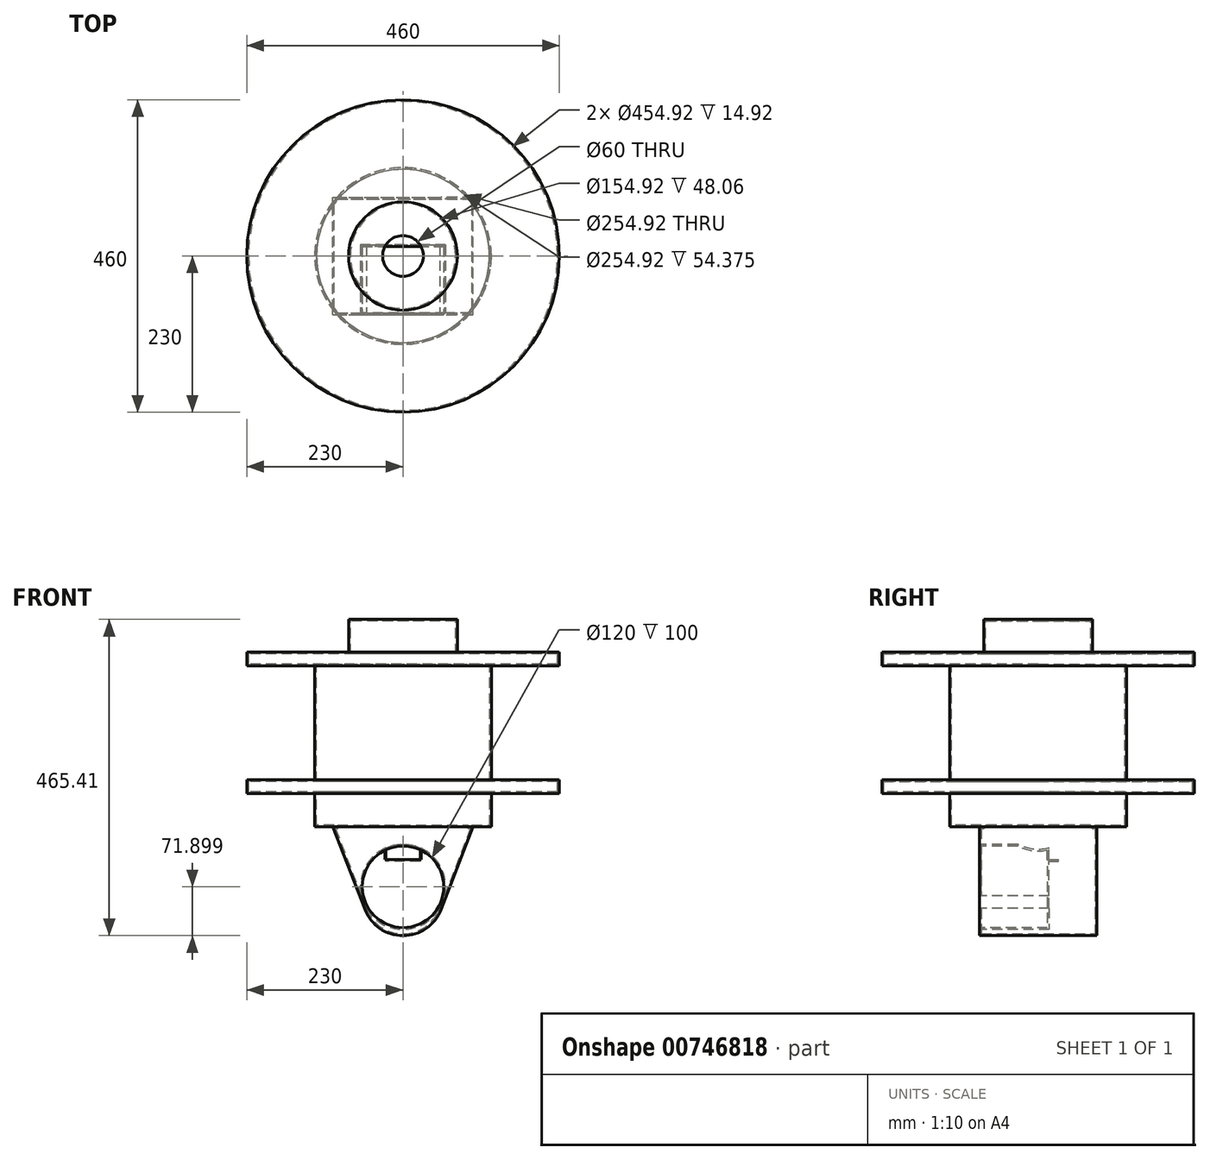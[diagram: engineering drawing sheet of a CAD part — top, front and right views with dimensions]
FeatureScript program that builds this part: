
annotation { "Feature Type Name" : "Feature", "Feature Type Description" : "" }
export const myFeature = defineFeature(function(context is Context, id is Id, definition is map)
    precondition{}
    {
        {
            var Q0;
            Q0=qCreatedBy(makeId("Front.planeOp"),FACE);
            var sketch = newSketch(context, id + "F0", { "sketchPlane" : qUnion([Q0])});
            skLineSegment(sketch, "E0", {"start": v(0, 412.84) * mm, "end": v(0, -278.5) * mm, "construction": true});
            skLineSegment(sketch, "E1", {"start": v(-30, 291.04) * mm, "end": v(-80, 291.04) * mm});
            skLineSegment(sketch, "E2", {"start": v(-80, 291.04) * mm, "end": v(-80, 242.99) * mm});
            skLineSegment(sketch, "E3", {"start": v(-80, 242.99) * mm, "end": v(-230, 242.99) * mm});
            skLineSegment(sketch, "E4", {"start": v(-230, 242.99) * mm, "end": v(-230, 222.99) * mm});
            skLineSegment(sketch, "E5", {"start": v(-230, 222.99) * mm, "end": v(-130, 222.99) * mm});
            skLineSegment(sketch, "E6", {"start": v(-130, 222.99) * mm, "end": v(-130, 54.93) * mm});
            skLineSegment(sketch, "E7", {"start": v(-130, 54.93) * mm, "end": v(-230, 54.93) * mm});
            skLineSegment(sketch, "E8", {"start": v(-230, 54.93) * mm, "end": v(-230, 34.93) * mm});
            skLineSegment(sketch, "E9", {"start": v(-230, 34.93) * mm, "end": v(-130, 34.93) * mm});
            skLineSegment(sketch, "E10", {"start": v(-130, 34.93) * mm, "end": v(-130, -14.37) * mm});
            skLineSegment(sketch, "E11", {"start": v(-130, -14.37) * mm, "end": v(-30, -14.37) * mm});
            skLineSegment(sketch, "E12", {"start": v(-30, -14.37) * mm, "end": v(-30, 291.04) * mm});
            skSolve(sketch);
        }
        {
            var Q0;
            Q0 = qSketchRegion(id + "F0", true);
            var Q1;
            Q1=sQuery(id+"F0.wireOp",EDGE,"E0");
            revolve(context, id + "F1", {"surfaceOperationType" : NewSurfaceOperationType.NEW, "entities" : qUnion([Q0]), "axis" : qUnion([Q1]), "revolveType" : RevolveType.FULL});
        }
        {
            var Q0;
            Q0=qCreatedBy(makeId("Front.planeOp"),FACE);
            var sketch = newSketch(context, id + "F2", { "sketchPlane" : qUnion([Q0])});
            skArc(sketch, "E13", {"start": v(-55.93, -136.08) * mm, "mid": v(0, -174.37) * mm, "end": v(55.93, -136.08) * mm});
            skLineSegment(sketch, "E14", {"start": v(103.17, -14.37) * mm, "end": v(55.93, -136.08) * mm});
            skLineSegment(sketch, "E15", {"start": v(-103.17, -14.37) * mm, "end": v(-55.93, -136.08) * mm});
            skLineSegment(sketch, "E16", {"start": v(0, 131.73) * mm, "end": v(0, -414.63) * mm, "construction": true});
            skLineSegment(sketch, "E17", {"start": v(-103.17, -14.37) * mm, "end": v(103.17, -14.37) * mm});
            skSolve(sketch);
        }
        {
            var Q0;
            Q0 = qSketchRegion(id + "F2", true);
            extrude(context, id + "F3", {"entities" : qUnion([Q0]), "operationType" : NewBodyOperationType.ADD, "endBound" : BoundingType.SYMMETRIC, "depth" : 172.72 * mm, "offsetDistance" : 25.4 * mm});
        }
        {
            var Q0;
            Q0=makeQuery(id+"F3.opExtrude","CAP_FACE",FACE,{"disambiguationData":[OSD([sQuery(id+"F2.wireOp",EDGE,"E13"),sQuery(id+"F2.wireOp",EDGE,"E14"),sQuery(id+"F2.wireOp",EDGE,"E15"),sQuery(id+"F2.wireOp",EDGE,"E17")])],"isStart":false});
            var sketch = newSketch(context, id + "F4", { "sketchPlane" : qUnion([Q0])});
            skCircle(sketch, "E18", {"center": v(0, -102.47) * mm, "radius": 60 * mm});
            skSolve(sketch);
        }
        {
            var Q0;
            Q0 = qSketchRegion(id + "F4", true);
            extrude(context, id + "F5", {"entities" : qUnion([Q0]), "operationType" : NewBodyOperationType.REMOVE, "oppositeDirection" : true, "depth" : 100 * mm, "offsetDistance" : 25.4 * mm});
        }
        {
            var Q0;
            Q0=makeQuery(id+"F3.boolean.opBoolean","SPLIT",FACE,{"disambiguationData":[TD([makeQuery(id+"F1.opRevolve","SWEPT_FACE",FACE,{"disambiguationData":[OSD([sQuery(id+"F0.wireOp",EDGE,"E12")])]})])],"derivedFrom":makeQuery(id+"F3.opExtrude","SWEPT_FACE",FACE,{"disambiguationData":[OSD([sQuery(id+"F2.wireOp",EDGE,"E17")])]})});
            var sketch = newSketch(context, id + "F6", { "sketchPlane" : qUnion([Q0])});
            skCircle(sketch, "E19", {"center": v(0, 0) * mm, "radius": 30 * mm});
            skSolve(sketch);
        }
        {
            var Q0;
            Q0 = qSketchRegion(id + "F6", true);
            extrude(context, id + "F7", {"entities" : qUnion([Q0]), "operationType" : NewBodyOperationType.REMOVE, "oppositeDirection" : true, "depth" : 48.26 * mm, "offsetDistance" : 25.4 * mm});
        }
        {
            var Q0;
            Q0=makeQuery(id+"F7.boolean.opBoolean","MERGE",FACE,{"derivedFrom":[makeQuery(id+"F1.opRevolve","SWEPT_FACE",FACE,{"disambiguationData":[OSD([sQuery(id+"F0.wireOp",EDGE,"E12")])]}),makeQuery(id+"F7.opExtrude","SWEPT_FACE",FACE,{"disambiguationData":[OSD([sQuery(id+"F6.wireOp",EDGE,"E19")])]})]});
            shell(context, id + "F8", {"entities" : qUnion([Q0]), "thickness" : 2.54 * mm});
        }
    });
